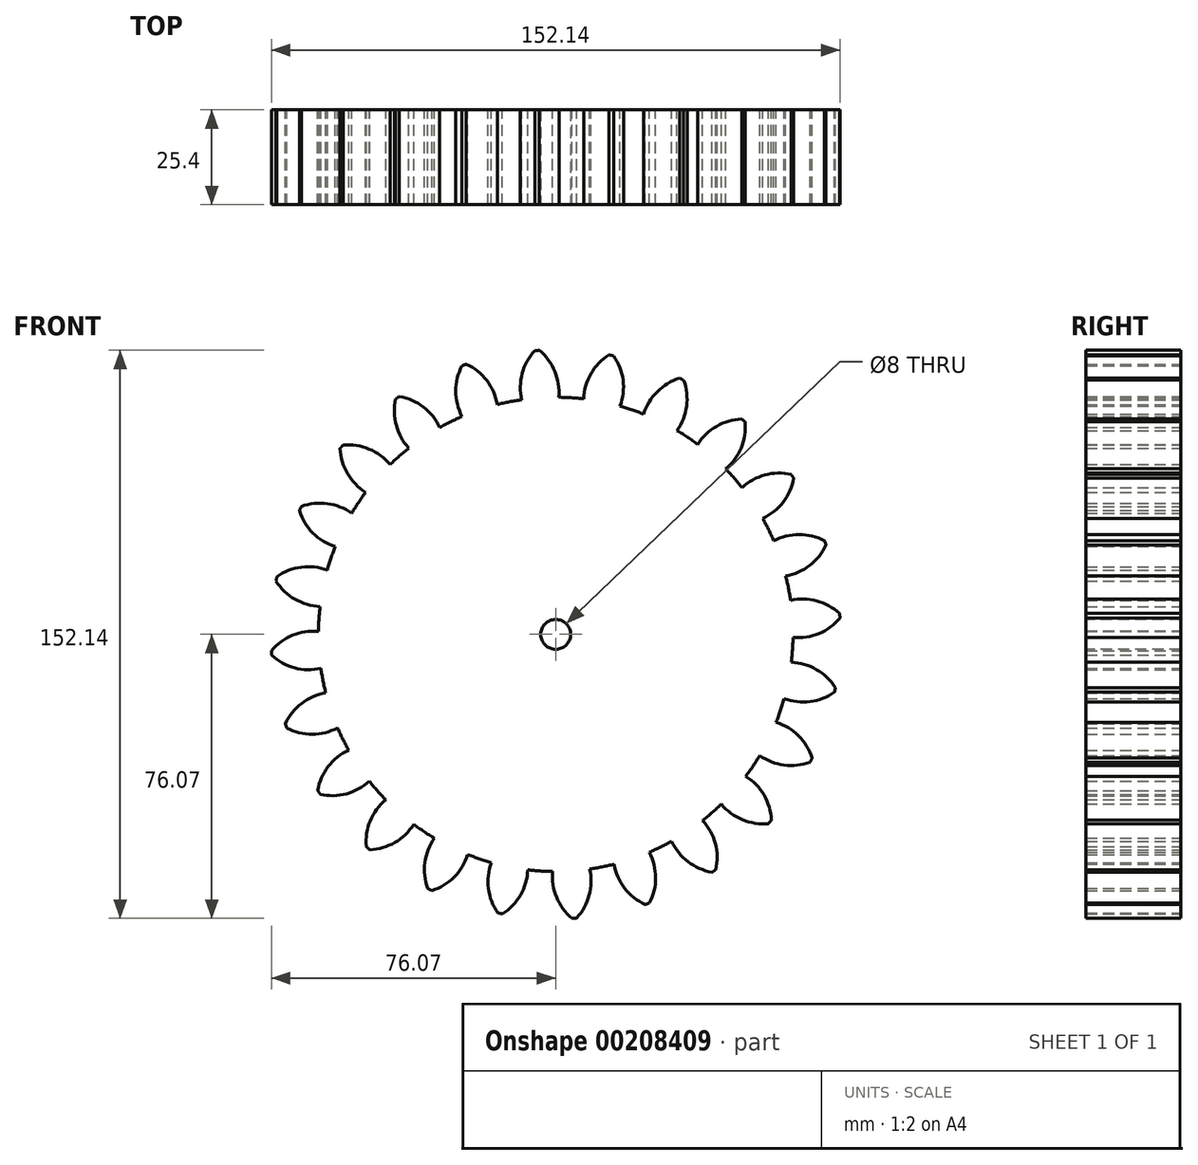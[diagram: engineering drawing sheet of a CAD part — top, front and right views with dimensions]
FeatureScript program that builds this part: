
annotation { "Feature Type Name" : "Feature", "Feature Type Description" : "" }
export const myFeature = defineFeature(function(context is Context, id is Id, definition is map)
    precondition{}
    {
        {
            var Q0;
            Q0=qCreatedBy(makeId("Front.planeOp"),FACE);
            var sketch = newSketch(context, id + "F0", { "sketchPlane" : qUnion([Q0])});
            skPoint(sketch, "E0.rect.middle", {"position": v(0, 0) * mm});
            skLineSegment(sketch, "E1", {"start": v(0, 0) * mm, "end": v(0, 76.2) * mm});
            skLineSegment(sketch, "E2", {"start": v(0, 0) * mm, "end": v(0, -76.2) * mm});
            skLineSegment(sketch, "E3", {"start": v(0, 0) * mm, "end": v(19.72, 73.6) * mm});
            skLineSegment(sketch, "E4", {"start": v(0, 0) * mm, "end": v(38.1, 66) * mm});
            skLineSegment(sketch, "E5", {"start": v(0, 0) * mm, "end": v(53.88, 53.88) * mm});
            skLineSegment(sketch, "E6", {"start": v(0, 0) * mm, "end": v(66, 38.1) * mm});
            skLineSegment(sketch, "E7", {"start": v(0, 0) * mm, "end": v(73.6, 19.72) * mm});
            skLineSegment(sketch, "E8", {"start": v(0, 0) * mm, "end": v(76.2, 0) * mm});
            skLineSegment(sketch, "E9", {"start": v(0, 0) * mm, "end": v(73.6, -19.72) * mm});
            skLineSegment(sketch, "E10", {"start": v(0, 0) * mm, "end": v(66, -38.1) * mm});
            skLineSegment(sketch, "E11", {"start": v(0, 0) * mm, "end": v(53.88, -53.88) * mm});
            skLineSegment(sketch, "E12", {"start": v(0, 0) * mm, "end": v(38.1, -66) * mm});
            skLineSegment(sketch, "E13", {"start": v(0, 0) * mm, "end": v(19.72, -73.6) * mm});
            skLineSegment(sketch, "E14", {"start": v(0, 0) * mm, "end": v(-19.72, -73.6) * mm});
            skLineSegment(sketch, "E15", {"start": v(0, 0) * mm, "end": v(-38.1, -66) * mm});
            skLineSegment(sketch, "E16", {"start": v(0, 0) * mm, "end": v(-53.88, -53.88) * mm});
            skLineSegment(sketch, "E17", {"start": v(0, 0) * mm, "end": v(-66, -38.1) * mm});
            skLineSegment(sketch, "E18", {"start": v(0, 0) * mm, "end": v(-73.6, -19.72) * mm});
            skLineSegment(sketch, "E19", {"start": v(0, 0) * mm, "end": v(-76.2, 0.07) * mm});
            skLineSegment(sketch, "E20", {"start": v(0, 0) * mm, "end": v(-73.6, 19.72) * mm});
            skLineSegment(sketch, "E21", {"start": v(0, 0) * mm, "end": v(-66, 38.1) * mm});
            skLineSegment(sketch, "E22", {"start": v(0, 0) * mm, "end": v(-53.88, 53.88) * mm});
            skLineSegment(sketch, "E23", {"start": v(0, 0) * mm, "end": v(-38.1, 66) * mm});
            skLineSegment(sketch, "E24", {"start": v(0, 0) * mm, "end": v(-19.72, 73.6) * mm});
            skCircle(sketch, "E25", {"center": v(0, 0) * mm, "radius": 76.2 * mm});
            skCircle(sketch, "E26", {"center": v(0, 0) * mm, "radius": 69.85 * mm});
            skCircle(sketch, "E27", {"center": v(0, 0) * mm, "radius": 63.5 * mm});
            skLineSegment(sketch, "E28", {"start": v(0, 0) * mm, "end": v(-4.98, 76.04) * mm});
            skLineSegment(sketch, "E29", {"start": v(0, 69.85) * mm, "end": v(-76.58, 69.85) * mm});
            skLineSegment(sketch, "E30", {"start": v(0, 69.85) * mm, "end": v(-76.5, 42) * mm});
            skLineSegment(sketch, "E31", {"start": v(-4.98, 76.04) * mm, "end": v(-7.15, 109.16) * mm});
            skLineSegment(sketch, "E32", {"start": v(0, 76.2) * mm, "end": v(0, 110.22) * mm});
            skCircle(sketch, "E33", {"center": v(0, 69.85) * mm, "radius": 14.6 * mm});
            skPoint(sketch, "E34", {"position": v(-13.72, 64.85) * mm});
            skArc(sketch, "E35", {"start": v(0.82, 63.5) * mm, "mid": v(-0.22, 70.43) * mm, "end": v(-4.37, 76.07) * mm});
            skArc(sketch, "E36.MirrorCS", {"start": v(-9.1, 62.84) * mm, "mid": v(-8.97, 69.85) * mm, "end": v(-5.6, 76) * mm});
            skSolve(sketch);
        }
        {
            var Q0;
            {var subQ1=sQuery(id+"F0.wireOp",EDGE,"E23");var subQ3=sQuery(id+"F0.wireOp",EDGE,"E27");var subQ4=makeQuery(id+"F0.imprint","INTERSECT",VERTEX,{"derivedFrom":[subQ1,subQ3]});Q0=makeQuery(id+"F0.imprint","IMPRINT",FACE,{"disambiguationData":[TD([[makeQuery(id+"F0.imprint","IMPRINT",EDGE,{"disambiguationData":[TD([[subQ4,1.0]])],"derivedFrom":subQ3}),1.0]])]});}
            var Q1;
            {var subQ1=sQuery(id+"F0.wireOp",EDGE,"E22");var subQ3=sQuery(id+"F0.wireOp",EDGE,"E27");var subQ4=makeQuery(id+"F0.imprint","INTERSECT",VERTEX,{"derivedFrom":[subQ1,subQ3]});Q1=makeQuery(id+"F0.imprint","IMPRINT",FACE,{"disambiguationData":[TD([[makeQuery(id+"F0.imprint","IMPRINT",EDGE,{"disambiguationData":[TD([[subQ4,1.0]])],"derivedFrom":subQ3}),1.0]])]});}
            var Q2;
            {var subQ1=sQuery(id+"F0.wireOp",EDGE,"E1");var subQ3=sQuery(id+"F0.wireOp",EDGE,"E33");var subQ4=makeQuery(id+"F0.imprint","INTERSECT",VERTEX,{"derivedFrom":[subQ1,subQ3]});Q2=makeQuery(id+"F0.imprint","IMPRINT",FACE,{"disambiguationData":[TD([[makeQuery(id+"F0.imprint","IMPRINT",EDGE,{"disambiguationData":[TD([[subQ4,1.0]])],"derivedFrom":subQ3}),-1.0]])]});}
            var Q3;
            {var subQ1=sQuery(id+"F0.wireOp",EDGE,"E19");var subQ3=sQuery(id+"F0.wireOp",EDGE,"E27");var subQ4=makeQuery(id+"F0.imprint","INTERSECT",VERTEX,{"derivedFrom":[subQ1,subQ3]});Q3=makeQuery(id+"F0.imprint","IMPRINT",FACE,{"disambiguationData":[TD([[makeQuery(id+"F0.imprint","IMPRINT",EDGE,{"disambiguationData":[TD([[subQ4,1.0]])],"derivedFrom":subQ3}),1.0]])]});}
            var Q4;
            {var subQ1=sQuery(id+"F0.wireOp",EDGE,"E24");var subQ3=sQuery(id+"F0.wireOp",EDGE,"E27");var subQ4=makeQuery(id+"F0.imprint","INTERSECT",VERTEX,{"derivedFrom":[subQ1,subQ3]});Q4=makeQuery(id+"F0.imprint","IMPRINT",FACE,{"disambiguationData":[TD([[makeQuery(id+"F0.imprint","IMPRINT",EDGE,{"disambiguationData":[TD([[subQ4,1.0]])],"derivedFrom":subQ3}),1.0]])]});}
            var Q5;
            {var subQ1=sQuery(id+"F0.wireOp",EDGE,"E20");var subQ3=sQuery(id+"F0.wireOp",EDGE,"E27");var subQ4=makeQuery(id+"F0.imprint","INTERSECT",VERTEX,{"derivedFrom":[subQ1,subQ3]});Q5=makeQuery(id+"F0.imprint","IMPRINT",FACE,{"disambiguationData":[TD([[makeQuery(id+"F0.imprint","IMPRINT",EDGE,{"disambiguationData":[TD([[subQ4,1.0]])],"derivedFrom":subQ3}),1.0]])]});}
            var Q6;
            {var subQ1=sQuery(id+"F0.wireOp",EDGE,"E21");var subQ3=sQuery(id+"F0.wireOp",EDGE,"E27");var subQ4=makeQuery(id+"F0.imprint","INTERSECT",VERTEX,{"derivedFrom":[subQ1,subQ3]});Q6=makeQuery(id+"F0.imprint","IMPRINT",FACE,{"disambiguationData":[TD([[makeQuery(id+"F0.imprint","IMPRINT",EDGE,{"disambiguationData":[TD([[subQ4,1.0]])],"derivedFrom":subQ3}),1.0]])]});}
            var Q7;
            {var subQ1=sQuery(id+"F0.wireOp",EDGE,"E6");var subQ3=sQuery(id+"F0.wireOp",EDGE,"E27");var subQ4=makeQuery(id+"F0.imprint","INTERSECT",VERTEX,{"derivedFrom":[subQ1,subQ3]});Q7=makeQuery(id+"F0.imprint","IMPRINT",FACE,{"disambiguationData":[TD([[makeQuery(id+"F0.imprint","IMPRINT",EDGE,{"disambiguationData":[TD([[subQ4,1.0]])],"derivedFrom":subQ3}),1.0]])]});}
            var Q8;
            {var subQ1=sQuery(id+"F0.wireOp",EDGE,"E4");var subQ3=sQuery(id+"F0.wireOp",EDGE,"E27");var subQ4=makeQuery(id+"F0.imprint","INTERSECT",VERTEX,{"derivedFrom":[subQ1,subQ3]});Q8=makeQuery(id+"F0.imprint","IMPRINT",FACE,{"disambiguationData":[TD([[makeQuery(id+"F0.imprint","IMPRINT",EDGE,{"disambiguationData":[TD([[subQ4,1.0]])],"derivedFrom":subQ3}),1.0]])]});}
            var Q9;
            {var subQ1=sQuery(id+"F0.wireOp",EDGE,"E7");var subQ3=sQuery(id+"F0.wireOp",EDGE,"E27");var subQ4=makeQuery(id+"F0.imprint","INTERSECT",VERTEX,{"derivedFrom":[subQ1,subQ3]});Q9=makeQuery(id+"F0.imprint","IMPRINT",FACE,{"disambiguationData":[TD([[makeQuery(id+"F0.imprint","IMPRINT",EDGE,{"disambiguationData":[TD([[subQ4,1.0]])],"derivedFrom":subQ3}),1.0]])]});}
            var Q10;
            {var subQ0=sQuery(id+"F0.wireOp",EDGE,"E3");var subQ5=sQuery(id+"F0.wireOp",EDGE,"E27");var subQ6=makeQuery(id+"F0.imprint","INTERSECT",VERTEX,{"derivedFrom":[subQ0,subQ5]});Q10=makeQuery(id+"F0.imprint","IMPRINT",FACE,{"disambiguationData":[TD([[makeQuery(id+"F0.imprint","IMPRINT",EDGE,{"disambiguationData":[TD([[subQ6,-1.0]])],"derivedFrom":subQ5}),1.0]])]});}
            var Q11;
            {var subQ1=sQuery(id+"F0.wireOp",EDGE,"E3");var subQ3=sQuery(id+"F0.wireOp",EDGE,"E27");var subQ4=makeQuery(id+"F0.imprint","INTERSECT",VERTEX,{"derivedFrom":[subQ1,subQ3]});Q11=makeQuery(id+"F0.imprint","IMPRINT",FACE,{"disambiguationData":[TD([[makeQuery(id+"F0.imprint","IMPRINT",EDGE,{"disambiguationData":[TD([[subQ4,1.0]])],"derivedFrom":subQ3}),1.0]])]});}
            var Q12;
            {var subQ1=sQuery(id+"F0.wireOp",EDGE,"E5");var subQ3=sQuery(id+"F0.wireOp",EDGE,"E27");var subQ4=makeQuery(id+"F0.imprint","INTERSECT",VERTEX,{"derivedFrom":[subQ1,subQ3]});Q12=makeQuery(id+"F0.imprint","IMPRINT",FACE,{"disambiguationData":[TD([[makeQuery(id+"F0.imprint","IMPRINT",EDGE,{"disambiguationData":[TD([[subQ4,1.0]])],"derivedFrom":subQ3}),1.0]])]});}
            var Q13;
            {var subQ1=sQuery(id+"F0.wireOp",EDGE,"E17");var subQ3=sQuery(id+"F0.wireOp",EDGE,"E27");var subQ4=makeQuery(id+"F0.imprint","INTERSECT",VERTEX,{"derivedFrom":[subQ1,subQ3]});Q13=makeQuery(id+"F0.imprint","IMPRINT",FACE,{"disambiguationData":[TD([[makeQuery(id+"F0.imprint","IMPRINT",EDGE,{"disambiguationData":[TD([[subQ4,1.0]])],"derivedFrom":subQ3}),1.0]])]});}
            var Q14;
            {var subQ1=sQuery(id+"F0.wireOp",EDGE,"E15");var subQ3=sQuery(id+"F0.wireOp",EDGE,"E27");var subQ4=makeQuery(id+"F0.imprint","INTERSECT",VERTEX,{"derivedFrom":[subQ1,subQ3]});Q14=makeQuery(id+"F0.imprint","IMPRINT",FACE,{"disambiguationData":[TD([[makeQuery(id+"F0.imprint","IMPRINT",EDGE,{"disambiguationData":[TD([[subQ4,1.0]])],"derivedFrom":subQ3}),1.0]])]});}
            var Q15;
            {var subQ1=sQuery(id+"F0.wireOp",EDGE,"E16");var subQ3=sQuery(id+"F0.wireOp",EDGE,"E27");var subQ4=makeQuery(id+"F0.imprint","INTERSECT",VERTEX,{"derivedFrom":[subQ1,subQ3]});Q15=makeQuery(id+"F0.imprint","IMPRINT",FACE,{"disambiguationData":[TD([[makeQuery(id+"F0.imprint","IMPRINT",EDGE,{"disambiguationData":[TD([[subQ4,1.0]])],"derivedFrom":subQ3}),1.0]])]});}
            var Q16;
            {var subQ1=sQuery(id+"F0.wireOp",EDGE,"E2");var subQ3=sQuery(id+"F0.wireOp",EDGE,"E27");var subQ4=makeQuery(id+"F0.imprint","INTERSECT",VERTEX,{"derivedFrom":[subQ1,subQ3]});Q16=makeQuery(id+"F0.imprint","IMPRINT",FACE,{"disambiguationData":[TD([[makeQuery(id+"F0.imprint","IMPRINT",EDGE,{"disambiguationData":[TD([[subQ4,1.0]])],"derivedFrom":subQ3}),1.0]])]});}
            var Q17;
            {var subQ1=sQuery(id+"F0.wireOp",EDGE,"E14");var subQ3=sQuery(id+"F0.wireOp",EDGE,"E27");var subQ4=makeQuery(id+"F0.imprint","INTERSECT",VERTEX,{"derivedFrom":[subQ1,subQ3]});Q17=makeQuery(id+"F0.imprint","IMPRINT",FACE,{"disambiguationData":[TD([[makeQuery(id+"F0.imprint","IMPRINT",EDGE,{"disambiguationData":[TD([[subQ4,1.0]])],"derivedFrom":subQ3}),1.0]])]});}
            var Q18;
            {var subQ1=sQuery(id+"F0.wireOp",EDGE,"E18");var subQ3=sQuery(id+"F0.wireOp",EDGE,"E27");var subQ4=makeQuery(id+"F0.imprint","INTERSECT",VERTEX,{"derivedFrom":[subQ1,subQ3]});Q18=makeQuery(id+"F0.imprint","IMPRINT",FACE,{"disambiguationData":[TD([[makeQuery(id+"F0.imprint","IMPRINT",EDGE,{"disambiguationData":[TD([[subQ4,1.0]])],"derivedFrom":subQ3}),1.0]])]});}
            var Q19;
            {var subQ0=sQuery(id+"F0.wireOp",EDGE,"E33");var subQ1=sQuery(id+"F0.wireOp",EDGE,"E1");var subQ2=makeQuery(id+"F0.imprint","INTERSECT",VERTEX,{"derivedFrom":[subQ1,subQ0]});Q19=makeQuery(id+"F0.imprint","IMPRINT",FACE,{"disambiguationData":[TD([[makeQuery(id+"F0.imprint","IMPRINT",EDGE,{"disambiguationData":[TD([[subQ2,-1.0]])],"derivedFrom":subQ1}),1.0]])]});}
            var Q20;
            {var subQ0=sQuery(id+"F0.wireOp",EDGE,"E27");var subQ1=makeQuery(id+"F0.imprint","INTERSECT",VERTEX,{"derivedFrom":[subQ0,sQuery(id+"F0.wireOp",EDGE,"E36.MirrorCS")]});Q20=makeQuery(id+"F0.imprint","IMPRINT",FACE,{"disambiguationData":[TD([[makeQuery(id+"F0.imprint","IMPRINT",EDGE,{"disambiguationData":[TD([[subQ1,1.0]])],"derivedFrom":subQ0}),1.0]])]});}
            var Q21;
            {var subQ0=sQuery(id+"F0.wireOp",EDGE,"E33");var subQ1=sQuery(id+"F0.wireOp",EDGE,"E1");var subQ2=makeQuery(id+"F0.imprint","INTERSECT",VERTEX,{"derivedFrom":[subQ1,subQ0]});Q21=makeQuery(id+"F0.imprint","IMPRINT",FACE,{"disambiguationData":[TD([[makeQuery(id+"F0.imprint","IMPRINT",EDGE,{"disambiguationData":[TD([[subQ2,-1.0]])],"derivedFrom":subQ1}),-1.0]])]});}
            var Q22;
            {var subQ1=sQuery(id+"F0.wireOp",EDGE,"E1");var subQ3=sQuery(id+"F0.wireOp",EDGE,"E27");var subQ4=makeQuery(id+"F0.imprint","INTERSECT",VERTEX,{"derivedFrom":[subQ1,subQ3]});Q22=makeQuery(id+"F0.imprint","IMPRINT",FACE,{"disambiguationData":[TD([[makeQuery(id+"F0.imprint","IMPRINT",EDGE,{"disambiguationData":[TD([[subQ4,-1.0]])],"derivedFrom":subQ3}),-1.0]])]});}
            var Q23;
            {var subQ0=sQuery(id+"F0.wireOp",EDGE,"E36.MirrorCS");var subQ1=sQuery(id+"F0.wireOp",EDGE,"E27");var subQ2=makeQuery(id+"F0.imprint","INTERSECT",VERTEX,{"derivedFrom":[subQ1,subQ0]});Q23=makeQuery(id+"F0.imprint","IMPRINT",FACE,{"disambiguationData":[TD([[makeQuery(id+"F0.imprint","IMPRINT",EDGE,{"disambiguationData":[TD([[subQ2,1.0]])],"derivedFrom":subQ1}),-1.0]])]});}
            var Q24;
            {var subQ0=sQuery(id+"F0.wireOp",EDGE,"E28");var subQ1=sQuery(id+"F0.wireOp",EDGE,"E26");var subQ2=makeQuery(id+"F0.imprint","INTERSECT",VERTEX,{"derivedFrom":[subQ1,subQ0]});Q24=makeQuery(id+"F0.imprint","IMPRINT",FACE,{"disambiguationData":[TD([[makeQuery(id+"F0.imprint","IMPRINT",EDGE,{"disambiguationData":[TD([[subQ2,-1.0]])],"derivedFrom":subQ1}),1.0]])]});}
            var Q25;
            {var subQ0=sQuery(id+"F0.wireOp",EDGE,"E28");var subQ1=sQuery(id+"F0.wireOp",EDGE,"E26");var subQ2=makeQuery(id+"F0.imprint","INTERSECT",VERTEX,{"derivedFrom":[subQ1,subQ0]});Q25=makeQuery(id+"F0.imprint","IMPRINT",FACE,{"disambiguationData":[TD([[makeQuery(id+"F0.imprint","IMPRINT",EDGE,{"disambiguationData":[TD([[subQ2,-1.0]])],"derivedFrom":subQ1}),-1.0]])]});}
            var Q26;
            {var subQ0=sQuery(id+"F0.wireOp",EDGE,"E28");var subQ5=sQuery(id+"F0.wireOp",EDGE,"E29");var subQ6=makeQuery(id+"F0.imprint","INTERSECT",VERTEX,{"derivedFrom":[subQ0,subQ5]});Q26=makeQuery(id+"F0.imprint","IMPRINT",FACE,{"disambiguationData":[TD([[makeQuery(id+"F0.imprint","IMPRINT",EDGE,{"disambiguationData":[TD([[subQ6,-1.0]])],"derivedFrom":subQ5}),-1.0]])]});}
            var Q27;
            {var subQ1=sQuery(id+"F0.wireOp",EDGE,"E25");var subQ3=sQuery(id+"F0.wireOp",EDGE,"E35");var subQ4=makeQuery(id+"F0.imprint","INTERSECT",VERTEX,{"derivedFrom":[subQ1,subQ3]});Q27=makeQuery(id+"F0.imprint","IMPRINT",FACE,{"disambiguationData":[TD([[makeQuery(id+"F0.imprint","IMPRINT",EDGE,{"disambiguationData":[TD([[subQ4,-1.0]])],"derivedFrom":subQ1}),1.0]])]});}
            var Q28;
            {var subQ0=sQuery(id+"F0.wireOp",EDGE,"E35");var subQ3=sQuery(id+"F0.wireOp",EDGE,"E27");var subQ5=makeQuery(id+"F0.imprint","INTERSECT",VERTEX,{"derivedFrom":[subQ3,subQ0]});Q28=makeQuery(id+"F0.imprint","IMPRINT",FACE,{"disambiguationData":[TD([[makeQuery(id+"F0.imprint","IMPRINT",EDGE,{"disambiguationData":[TD([[subQ5,-1.0]])],"derivedFrom":subQ3}),-1.0]])]});}
            var Q29;
            {var subQ1=sQuery(id+"F0.wireOp",EDGE,"E26");var subQ3=sQuery(id+"F0.wireOp",EDGE,"E28");var subQ4=makeQuery(id+"F0.imprint","INTERSECT",VERTEX,{"derivedFrom":[subQ1,subQ3]});Q29=makeQuery(id+"F0.imprint","IMPRINT",FACE,{"disambiguationData":[TD([[makeQuery(id+"F0.imprint","IMPRINT",EDGE,{"disambiguationData":[TD([[subQ4,-1.0]])],"derivedFrom":subQ3}),-1.0]])]});}
            var Q30;
            {var subQ1=sQuery(id+"F0.wireOp",EDGE,"E26");var subQ3=sQuery(id+"F0.wireOp",EDGE,"E28");var subQ4=makeQuery(id+"F0.imprint","INTERSECT",VERTEX,{"derivedFrom":[subQ1,subQ3]});Q30=makeQuery(id+"F0.imprint","IMPRINT",FACE,{"disambiguationData":[TD([[makeQuery(id+"F0.imprint","IMPRINT",EDGE,{"disambiguationData":[TD([[subQ4,1.0]])],"derivedFrom":subQ3}),-1.0]])]});}
            var Q31;
            {var subQ1=sQuery(id+"F0.wireOp",EDGE,"E10");var subQ3=sQuery(id+"F0.wireOp",EDGE,"E27");var subQ4=makeQuery(id+"F0.imprint","INTERSECT",VERTEX,{"derivedFrom":[subQ1,subQ3]});Q31=makeQuery(id+"F0.imprint","IMPRINT",FACE,{"disambiguationData":[TD([[makeQuery(id+"F0.imprint","IMPRINT",EDGE,{"disambiguationData":[TD([[subQ4,1.0]])],"derivedFrom":subQ3}),1.0]])]});}
            var Q32;
            {var subQ1=sQuery(id+"F0.wireOp",EDGE,"E9");var subQ3=sQuery(id+"F0.wireOp",EDGE,"E27");var subQ4=makeQuery(id+"F0.imprint","INTERSECT",VERTEX,{"derivedFrom":[subQ1,subQ3]});Q32=makeQuery(id+"F0.imprint","IMPRINT",FACE,{"disambiguationData":[TD([[makeQuery(id+"F0.imprint","IMPRINT",EDGE,{"disambiguationData":[TD([[subQ4,1.0]])],"derivedFrom":subQ3}),1.0]])]});}
            var Q33;
            {var subQ1=sQuery(id+"F0.wireOp",EDGE,"E8");var subQ3=sQuery(id+"F0.wireOp",EDGE,"E27");var subQ4=makeQuery(id+"F0.imprint","INTERSECT",VERTEX,{"derivedFrom":[subQ1,subQ3]});Q33=makeQuery(id+"F0.imprint","IMPRINT",FACE,{"disambiguationData":[TD([[makeQuery(id+"F0.imprint","IMPRINT",EDGE,{"disambiguationData":[TD([[subQ4,1.0]])],"derivedFrom":subQ3}),1.0]])]});}
            var Q34;
            {var subQ1=sQuery(id+"F0.wireOp",EDGE,"E11");var subQ3=sQuery(id+"F0.wireOp",EDGE,"E27");var subQ4=makeQuery(id+"F0.imprint","INTERSECT",VERTEX,{"derivedFrom":[subQ1,subQ3]});Q34=makeQuery(id+"F0.imprint","IMPRINT",FACE,{"disambiguationData":[TD([[makeQuery(id+"F0.imprint","IMPRINT",EDGE,{"disambiguationData":[TD([[subQ4,1.0]])],"derivedFrom":subQ3}),1.0]])]});}
            var Q35;
            {var subQ1=sQuery(id+"F0.wireOp",EDGE,"E2");var subQ3=sQuery(id+"F0.wireOp",EDGE,"E27");var subQ4=makeQuery(id+"F0.imprint","INTERSECT",VERTEX,{"derivedFrom":[subQ1,subQ3]});Q35=makeQuery(id+"F0.imprint","IMPRINT",FACE,{"disambiguationData":[TD([[makeQuery(id+"F0.imprint","IMPRINT",EDGE,{"disambiguationData":[TD([[subQ4,-1.0]])],"derivedFrom":subQ3}),1.0]])]});}
            var Q36;
            {var subQ1=sQuery(id+"F0.wireOp",EDGE,"E12");var subQ3=sQuery(id+"F0.wireOp",EDGE,"E27");var subQ4=makeQuery(id+"F0.imprint","INTERSECT",VERTEX,{"derivedFrom":[subQ1,subQ3]});Q36=makeQuery(id+"F0.imprint","IMPRINT",FACE,{"disambiguationData":[TD([[makeQuery(id+"F0.imprint","IMPRINT",EDGE,{"disambiguationData":[TD([[subQ4,1.0]])],"derivedFrom":subQ3}),1.0]])]});}
            extrude(context, id + "F1", {"entities" : qUnion([Q0, Q1, Q2, Q3, Q4, Q5, Q6, Q7, Q8, Q9, Q10, Q11, Q12, Q13, Q14, Q15, Q16, Q17, Q18, Q19, Q20, Q21, Q22, Q23, Q24, Q25, Q26, Q27, Q28, Q29, Q30, Q31, Q32, Q33, Q34, Q35, Q36]), "depth" : 25.4 * mm, "symmetric" : true});
        }
        {
            var Q0;
            Q0=makeQuery(id+"F1.opExtrude","SWEPT_BODY",BODY,{"disambiguationData":[OSD([sQuery(id+"F0.wireOp",EDGE,"E25"),sQuery(id+"F0.wireOp",EDGE,"E27"),sQuery(id+"F0.wireOp",EDGE,"E35"),sQuery(id+"F0.wireOp",EDGE,"E36.MirrorCS")])]});
            var Q1;
            Q1=makeQuery(id+"F1.opExtrude","SWEPT_FACE",FACE,{"disambiguationData":[OSD([sQuery(id+"F0.wireOp",EDGE,"E27")])]});
            circularPattern(context, id + "F2", {"operationType" : NewBodyOperationType.ADD, "entities" : qUnion([Q0]), "axis" : qUnion([Q1]), "angle" : 15 * degree, "instanceCount" : 24});
        }
        {
            var Q0;
            Q0=makeQuery(id+"F1.opExtrude","CAP_FACE",FACE,{"disambiguationData":[OSD([sQuery(id+"F0.wireOp",EDGE,"E25"),sQuery(id+"F0.wireOp",EDGE,"E27"),sQuery(id+"F0.wireOp",EDGE,"E35"),sQuery(id+"F0.wireOp",EDGE,"E36.MirrorCS")])],"isStart":false});
            var sketch = newSketch(context, id + "F3", { "sketchPlane" : qUnion([Q0])});
            skPoint(sketch, "E37", {"position": v(0, 0) * mm});
            skSolve(sketch);
        }
        {
            var Q0;
            Q0=sQuery(id+"F3.wireOp",VERTEX,"E37");
            var Q1;
            Q1=makeQuery(id+"F1.opExtrude","SWEPT_BODY",BODY,{"disambiguationData":[OSD([sQuery(id+"F0.wireOp",EDGE,"E25"),sQuery(id+"F0.wireOp",EDGE,"E27"),sQuery(id+"F0.wireOp",EDGE,"E35"),sQuery(id+"F0.wireOp",EDGE,"E36.MirrorCS")])]});
            hole(context, id + "F4", {"style" : HoleStyle.SIMPLE, "holeDiameter" : 8 * mm, "endStyle" : HoleEndStyle.THROUGH, "locations" : qUnion([Q0]), "scope" : qUnion([Q1]), "tappedDepth" : 12 * mm, "tapClearance" : 3});
        }
    });
